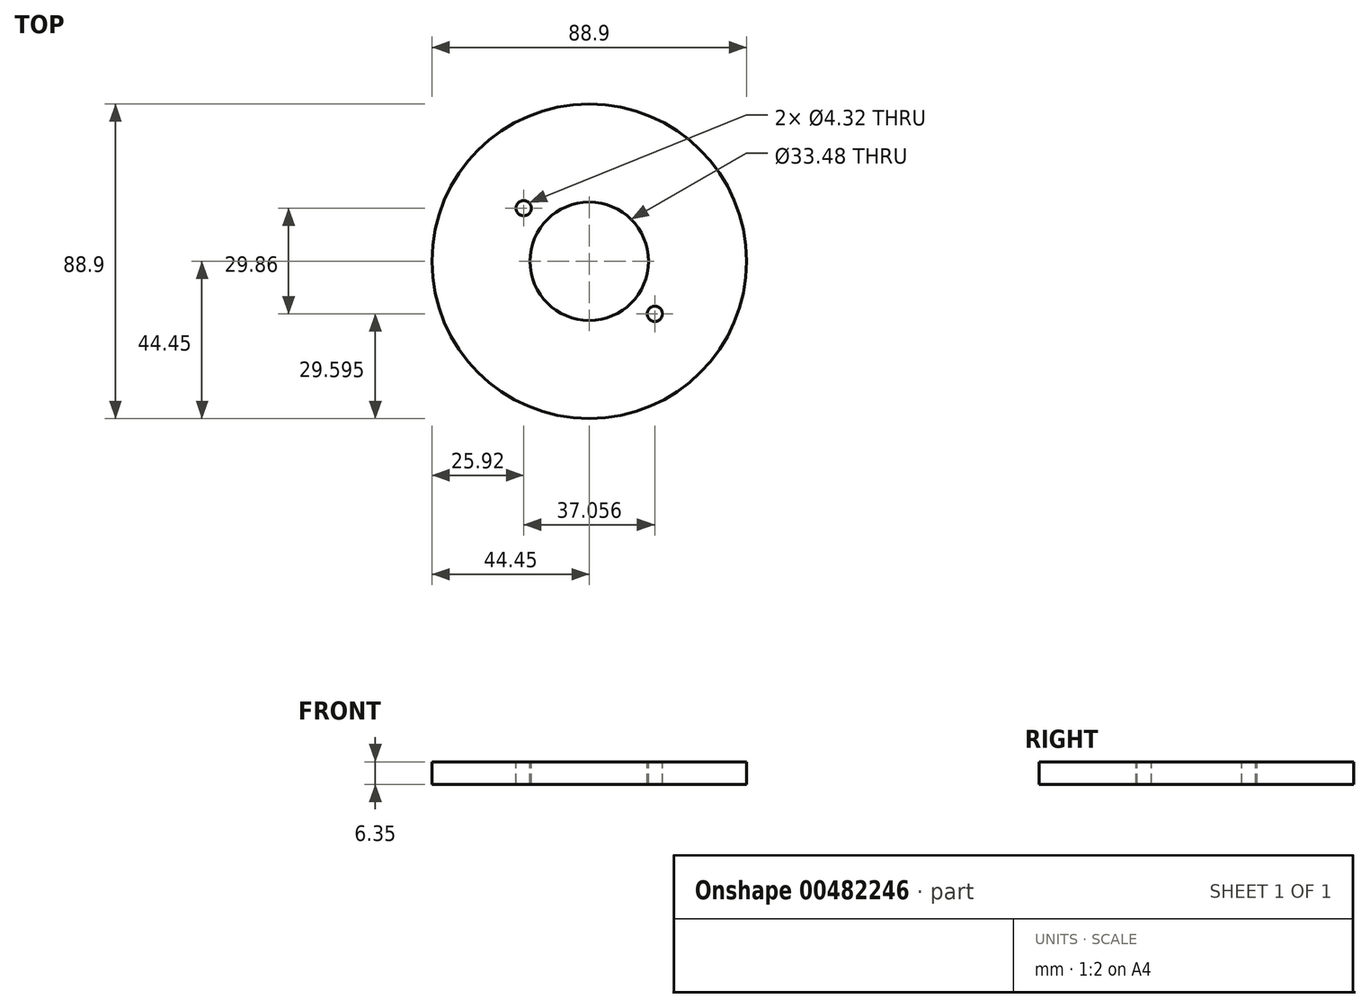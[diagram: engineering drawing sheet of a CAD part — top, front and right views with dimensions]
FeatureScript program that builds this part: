
annotation { "Feature Type Name" : "Feature", "Feature Type Description" : "" }
export const myFeature = defineFeature(function(context is Context, id is Id, definition is map)
    precondition{}
    {
        {
            var Q0;
            Q0=qCreatedBy(makeId("Top.planeOp"),FACE);
            var sketch = newSketch(context, id + "F0", { "sketchPlane" : qUnion([Q0])});
            skCircle(sketch, "E0", {"center": v(0, 0) * mm, "radius": 44.45 * mm});
            skSolve(sketch);
        }
        {
            var Q0;
            Q0=makeQuery(id+"F0.imprint","IMPRINT",FACE,{"disambiguationData":[TD([[makeQuery(id+"F0.imprint","IMPRINT",EDGE,{"derivedFrom":sQuery(id+"F0.wireOp",EDGE,"E0")}),1.0]])]});
            extrude(context, id + "F1", {"entities" : qUnion([Q0]), "depth" : 6.35 * mm});
        }
        {
            var Q0;
            Q0=makeQuery(id+"F1.opExtrude","CAP_FACE",FACE,{"disambiguationData":[OSD([sQuery(id+"F0.wireOp",EDGE,"E0")])],"isStart":false});
            var sketch = newSketch(context, id + "F2", { "sketchPlane" : qUnion([Q0])});
            skCircle(sketch, "E1", {"center": v(0, 0) * mm, "radius": 16.74 * mm});
            skSolve(sketch);
        }
        {
            var Q0;
            Q0=makeQuery(id+"F2.imprint","IMPRINT",FACE,{"disambiguationData":[TD([[makeQuery(id+"F2.imprint","IMPRINT",EDGE,{"derivedFrom":sQuery(id+"F2.wireOp",EDGE,"E1")}),1.0]])]});
            extrude(context, id + "F3", {"entities" : qUnion([Q0]), "operationType" : NewBodyOperationType.REMOVE, "oppositeDirection" : true, "depth" : 6.35 * mm});
        }
        {
            var Q0;
            Q0=qCreatedBy(makeId("Top.planeOp"),FACE);
            var sketch = newSketch(context, id + "F4", { "sketchPlane" : qUnion([Q0])});
            skCircle(sketch, "E2", {"center": v(0, 0) * mm, "radius": 27.94 * mm});
            skSolve(sketch);
        }
        {
            var Q0;
            Q0=makeQuery(id+"F4.imprint","IMPRINT",FACE,{"disambiguationData":[TD([[makeQuery(id+"F4.imprint","IMPRINT",EDGE,{"derivedFrom":sQuery(id+"F4.wireOp",EDGE,"E2")}),1.0]])]});
            var sketch = newSketch(context, id + "F5", { "sketchPlane" : qUnion([Q0])});
            skCircle(sketch, "E3", {"center": v(0, 0) * mm, "radius": 23.81 * mm});
            skSolve(sketch);
        }
        {
            var Q0;
            Q0=makeQuery(id+"F4.imprint","IMPRINT",FACE,{"disambiguationData":[TD([[makeQuery(id+"F4.imprint","IMPRINT",EDGE,{"derivedFrom":sQuery(id+"F4.wireOp",EDGE,"E2")}),1.0]])]});
            var sketch = newSketch(context, id + "F6", { "sketchPlane" : qUnion([Q0])});
            skLineSegment(sketch, "E4", {"start": v(-23.4, 18.86) * mm, "end": v(35.93, -28.95) * mm});
            skSolve(sketch);
        }
        {
            var Q0;
            Q0=makeQuery(id+"F1.opExtrude","CAP_FACE",FACE,{"disambiguationData":[OSD([sQuery(id+"F0.wireOp",EDGE,"E0")])],"isStart":false});
            var sketch = newSketch(context, id + "F7", { "sketchPlane" : qUnion([Q0])});
            skCircle(sketch, "E5", {"center": v(-18.53, 15) * mm, "radius": 2.16 * mm});
            skSolve(sketch);
        }
        {
            var Q0;
            Q0=makeQuery(id+"F7.imprint","IMPRINT",FACE,{"disambiguationData":[TD([[makeQuery(id+"F7.imprint","IMPRINT",EDGE,{"derivedFrom":sQuery(id+"F7.wireOp",EDGE,"E5")}),1.0]])]});
            extrude(context, id + "F8", {"entities" : qUnion([Q0]), "operationType" : NewBodyOperationType.REMOVE, "oppositeDirection" : true, "depth" : 6.35 * mm});
        }
        {
            var Q0;
            Q0=makeQuery(id+"F1.opExtrude","CAP_FACE",FACE,{"disambiguationData":[OSD([sQuery(id+"F0.wireOp",EDGE,"E0")])],"isStart":false});
            var sketch = newSketch(context, id + "F9", { "sketchPlane" : qUnion([Q0])});
            skCircle(sketch, "E6", {"center": v(18.53, -14.85) * mm, "radius": 2.16 * mm});
            skSolve(sketch);
        }
        {
            var Q0;
            Q0=makeQuery(id+"F9.imprint","IMPRINT",FACE,{"disambiguationData":[TD([[makeQuery(id+"F9.imprint","IMPRINT",EDGE,{"derivedFrom":sQuery(id+"F9.wireOp",EDGE,"E6")}),1.0]])]});
            extrude(context, id + "F10", {"entities" : qUnion([Q0]), "operationType" : NewBodyOperationType.REMOVE, "oppositeDirection" : true, "depth" : 6.35 * mm});
        }
    });
